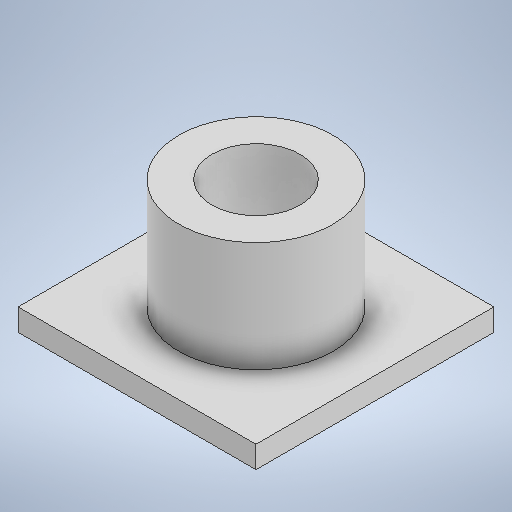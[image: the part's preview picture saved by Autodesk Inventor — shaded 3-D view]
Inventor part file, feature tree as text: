
AUTODESK INVENTOR PART (.ipt)
format: ipt  version: 2025 (Build 290162000, 162)  size: 235,008 bytes
history: native  units: mm
features: extrude x2, other x1, sketch x1
ambient origin geometry x8: Origin, YZ Plane, XZ Plane, XY Plane, X Axis, Y Axis, Z Axis, Center Point
bodies: Body1 (feature_tree)
feature tree (4):
  other  "Bryła1"
  sketch  "Szkic1"
  extrude  "Wyciągnięcie proste1"  Depth=20.0mm
  extrude  "Wyciągnięcie proste2"  Depth=54.0mm
